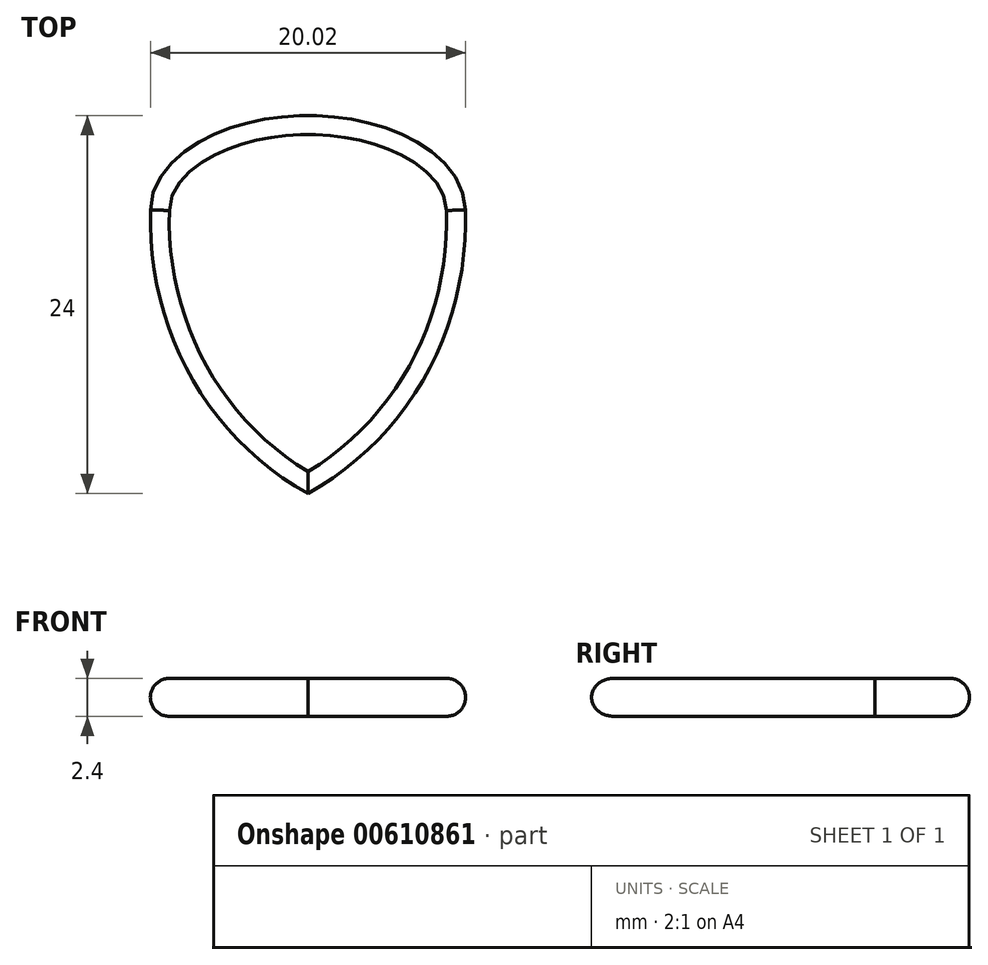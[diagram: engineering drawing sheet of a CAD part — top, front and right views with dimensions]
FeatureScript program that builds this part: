
annotation { "Feature Type Name" : "Feature", "Feature Type Description" : "" }
export const myFeature = defineFeature(function(context is Context, id is Id, definition is map)
    precondition{}
    {
        {
            var Q0;
            Q0=qCreatedBy(makeId("Top.planeOp"),FACE);
            var sketch = newSketch(context, id + "F0", { "sketchPlane" : qUnion([Q0])});
            skEllipticalArc(sketch, "E0", {});
            skEllipticalArc(sketch, "E1", {});
            skPoint(sketch, "E2", {"position": v(-39.9, 3.36) * mm});
            skPoint(sketch, "E3", {"position": v(-23.33, 3.36) * mm});
            skPoint(sketch, "E4", {"position": v(-21.61, 0) * mm});
            skEllipticalArc(sketch, "E5.trimOffspring", {});
            const initialGuessF0  = {"E0": [-0.03161151707172394, 0, 1, 0, 0.01, 0.006, 0, 3.141592653589793], "E1": [-0.04161151707172394, 0, 0.48564293117863244, -0.8741572761215376, 0.02059126028197401, 0.01982755325631149, 0, 1.0929807321065532], "E5.trimOffspring": [-0.021611517071723936, 0, -0.4856429311786319, -0.8741572761215379, 0.020591260281974, 0.01982755325631149, 5.190204575073031, 0]};
            skSetInitialGuess(sketch, initialGuessF0);
            skSolve(sketch);
        }
        {
            var Q0;
            Q0=qSketchRegion(id+"F0",true);
            var Q1;
            {var subQ1=sQuery(id+"F0.wireOp",EDGE,"E0");var subQ4=sQuery(id+"F0.wireOp",EDGE,"E1");var subQ6=makeQuery(id+"F0.imprint","INTERSECT",VERTEX,{"disambiguationData":[OD(1.0)],"derivedFrom":[subQ1,subQ4]});Q1=makeQuery(id+"F0.imprint","IMPRINT",FACE,{"disambiguationData":[TD([[makeQuery(id+"F0.imprint","IMPRINT",EDGE,{"disambiguationData":[TD([[subQ6,-1.0]])],"derivedFrom":subQ1}),1.0]])]});}
            extrude(context, id + "F1", {"entities" : qUnion([Q0, Q1]), "depth" : 2.4 * mm, "offsetDistance" : 25 * mm});
        }
        {
            var Q0;
            Q0=makeQuery(id+"F1.opExtrude","CAP_FACE",FACE,{"disambiguationData":[OSD([sQuery(id+"F0.wireOp",EDGE,"E0"),sQuery(id+"F0.wireOp",EDGE,"E1"),sQuery(id+"F0.wireOp",EDGE,"E5.trimOffspring")])],"isStart":false});
            var Q1;
            Q1=makeQuery(id+"F1.opExtrude","CAP_FACE",FACE,{"disambiguationData":[OSD([sQuery(id+"F0.wireOp",EDGE,"E0"),sQuery(id+"F0.wireOp",EDGE,"E1"),sQuery(id+"F0.wireOp",EDGE,"E5.trimOffspring")])],"isStart":true});
            fillet(context, id + "F2", {"entities" : qUnion([Q0, Q1]), "radius" : 1.2 * mm, "tangentPropagation" : true, "allowEdgeOverflow" : false});
        }
    });
